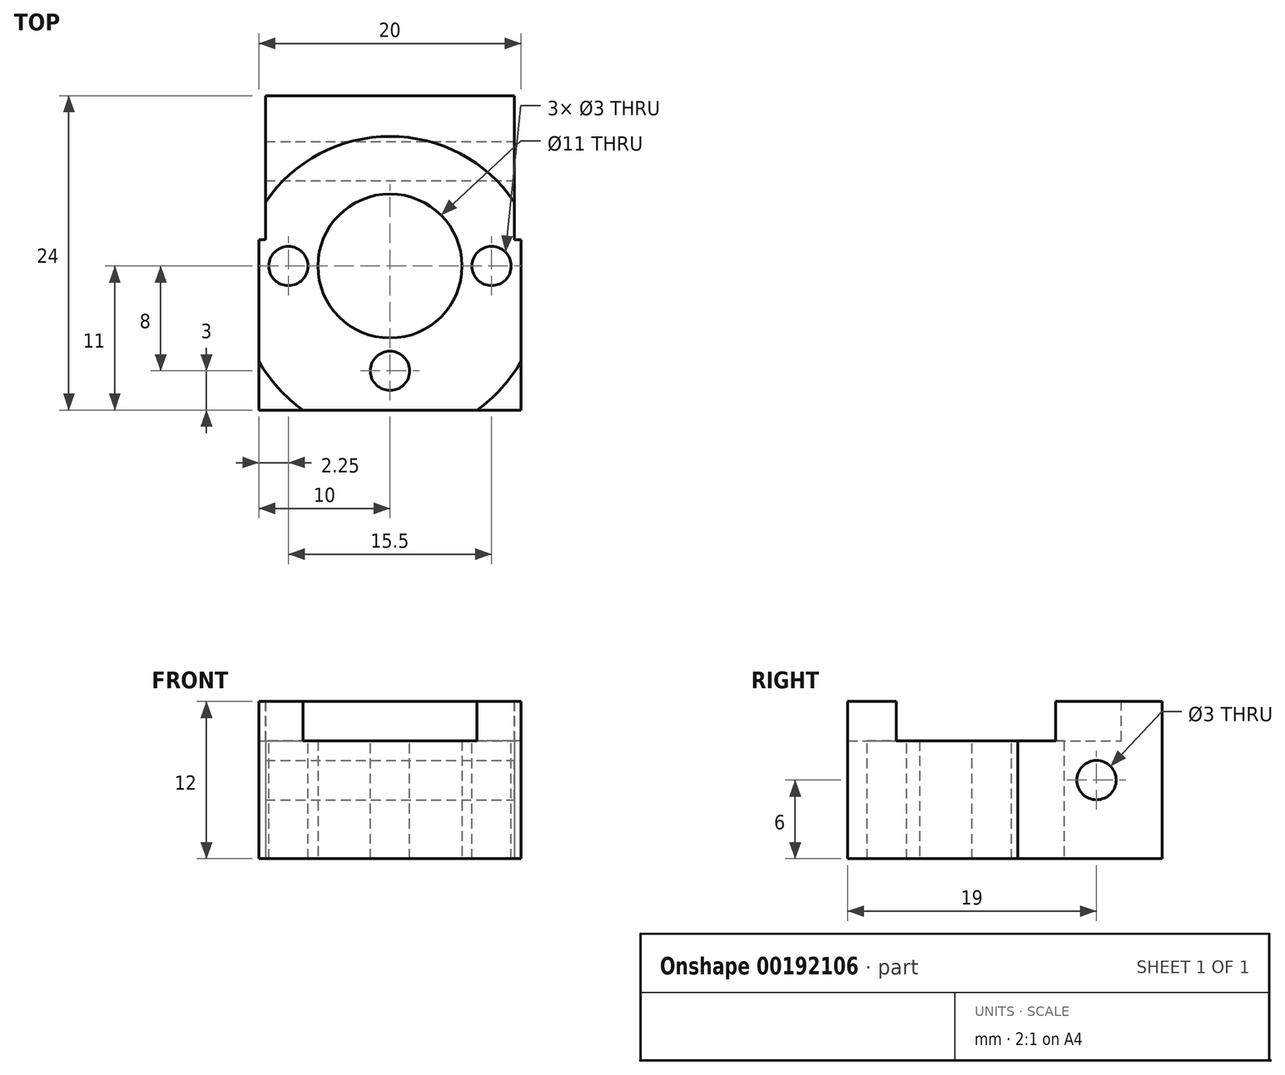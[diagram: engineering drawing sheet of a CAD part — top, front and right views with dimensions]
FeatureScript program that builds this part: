
annotation { "Feature Type Name" : "Feature", "Feature Type Description" : "" }
export const myFeature = defineFeature(function(context is Context, id is Id, definition is map)
    precondition{}
    {
        {
            var Q0;
            Q0=qCreatedBy(makeId("Top.planeOp"),FACE);
            var sketch = newSketch(context, id + "F0", { "sketchPlane" : qUnion([Q0])});
            skCircle(sketch, "E0", {"center": v(0, 0) * mm, "radius": 5.5 * mm});
            skLineSegment(sketch, "E1", {"start": v(9.5, 13) * mm, "end": v(-9.5, 13) * mm});
            skLineSegment(sketch, "E2", {"start": v(10, -11) * mm, "end": v(10, 2) * mm});
            skLineSegment(sketch, "E3", {"start": v(10, 2) * mm, "end": v(9.5, 2) * mm});
            skLineSegment(sketch, "E4", {"start": v(9.5, 2) * mm, "end": v(9.5, 13) * mm});
            skLineSegment(sketch, "E5", {"start": v(-10, -11) * mm, "end": v(-10, 2) * mm});
            skLineSegment(sketch, "E6", {"start": v(-10, 2) * mm, "end": v(-9.5, 2) * mm});
            skLineSegment(sketch, "E7", {"start": v(-9.5, 2) * mm, "end": v(-9.5, 13) * mm});
            skLineSegment(sketch, "E8", {"start": v(10, -11) * mm, "end": v(-10, -11) * mm});
            skSolve(sketch);
        }
        {
            var Q0;
            Q0=makeQuery(id+"F0.imprint","IMPRINT",FACE,{"disambiguationData":[TD([[makeQuery(id+"F0.imprint","IMPRINT",EDGE,{"derivedFrom":sQuery(id+"F0.wireOp",EDGE,"E0")}),-1.0]])]});
            extrude(context, id + "F1", {"entities" : qUnion([Q0]), "depth" : 12 * mm});
        }
        {
            var Q0;
            Q0=makeQuery(id+"F1.opExtrude","CAP_FACE",FACE,{"disambiguationData":[OSD([sQuery(id+"F0.wireOp",EDGE,"E0"),sQuery(id+"F0.wireOp",EDGE,"E1"),sQuery(id+"F0.wireOp",EDGE,"rkwbf3oP-30I9-U0Yv-dnpL-DhIv3d7Iuv3p"),sQuery(id+"F0.wireOp",EDGE,"po0v5kIw-LBBT-m3pm-F22V-GEr0gVHpED9w"),sQuery(id+"F0.wireOp",EDGE,"b044ZxhU-cJFl-NMno-NqXH-K3v0hHpDGOHu")])],"isStart":false});
            var sketch = newSketch(context, id + "F2", { "sketchPlane" : qUnion([Q0])});
            skCircle(sketch, "E9", {"center": v(0, -8) * mm, "radius": 1.5 * mm});
            skCircle(sketch, "E10", {"center": v(7.75, 0) * mm, "radius": 1.5 * mm});
            skCircle(sketch, "E11", {"center": v(-7.75, 0) * mm, "radius": 1.5 * mm});
            skSolve(sketch);
        }
        {
            var Q0;
            Q0=makeQuery(id+"F2.imprint","IMPRINT",FACE,{"disambiguationData":[TD([[makeQuery(id+"F2.imprint","IMPRINT",EDGE,{"derivedFrom":sQuery(id+"F2.wireOp",EDGE,"E10")}),1.0]])]});
            var Q1;
            Q1=makeQuery(id+"F2.imprint","IMPRINT",FACE,{"disambiguationData":[TD([[makeQuery(id+"F2.imprint","IMPRINT",EDGE,{"derivedFrom":sQuery(id+"F2.wireOp",EDGE,"E11")}),1.0]])]});
            var Q2;
            Q2=makeQuery(id+"F2.imprint","IMPRINT",FACE,{"disambiguationData":[TD([[makeQuery(id+"F2.imprint","IMPRINT",EDGE,{"derivedFrom":sQuery(id+"F2.wireOp",EDGE,"E9")}),1.0]])]});
            extrude(context, id + "F3", {"entities" : qUnion([Q0, Q1, Q2]), "operationType" : NewBodyOperationType.REMOVE, "oppositeDirection" : true, "depth" : 12 * mm});
        }
        {
            var Q0;
            Q0=makeQuery(id+"F1.opExtrude","SWEPT_FACE",FACE,{"disambiguationData":[OSD([sQuery(id+"F0.wireOp",EDGE,"E4")])]});
            var sketch = newSketch(context, id + "F4", { "sketchPlane" : qUnion([Q0])});
            skLineSegment(sketch, "E12", {"start": v(0, 0) * mm, "end": v(0, 6) * mm});
            skLineSegment(sketch, "E13", {"start": v(0, 6) * mm, "end": v(8, 6) * mm});
            skCircle(sketch, "E14", {"center": v(8, 6) * mm, "radius": 1.5 * mm});
            skSolve(sketch);
        }
        {
            var Q0;
            Q0=makeQuery(id+"F4.imprint","IMPRINT",FACE,{"disambiguationData":[TD([[makeQuery(id+"F4.imprint","IMPRINT",EDGE,{"derivedFrom":sQuery(id+"F4.wireOp",EDGE,"E14")}),1.0]])]});
            extrude(context, id + "F5", {"entities" : qUnion([Q0]), "operationType" : NewBodyOperationType.REMOVE, "oppositeDirection" : true, "depth" : 22 * mm});
        }
        {
            var Q0;
            Q0=makeQuery(id+"F1.opExtrude","CAP_FACE",FACE,{"disambiguationData":[OSD([sQuery(id+"F0.wireOp",EDGE,"E0"),sQuery(id+"F0.wireOp",EDGE,"E1"),sQuery(id+"F0.wireOp",EDGE,"E2"),sQuery(id+"F0.wireOp",EDGE,"E3"),sQuery(id+"F0.wireOp",EDGE,"E4"),sQuery(id+"F0.wireOp",EDGE,"E5"),sQuery(id+"F0.wireOp",EDGE,"E6"),sQuery(id+"F0.wireOp",EDGE,"E7"),sQuery(id+"F0.wireOp",EDGE,"E8")])],"isStart":false});
            var sketch = newSketch(context, id + "F6", { "sketchPlane" : qUnion([Q0])});
            skCircle(sketch, "E15", {"center": v(0, -1.6) * mm, "radius": 11.5 * mm});
            skSolve(sketch);
        }
        {
            var Q0;
            Q0 = qSketchRegion(id + "F6", true);
            extrude(context, id + "F7", {"entities" : qUnion([Q0]), "operationType" : NewBodyOperationType.REMOVE, "oppositeDirection" : true, "depth" : 3 * mm});
        }
    });
